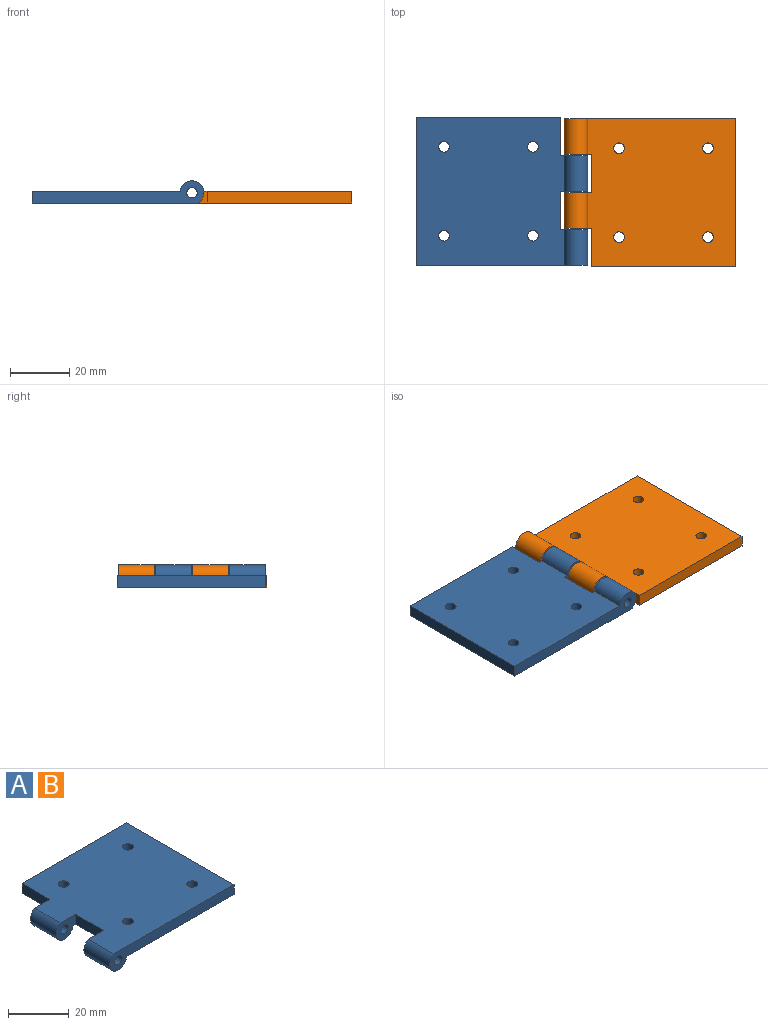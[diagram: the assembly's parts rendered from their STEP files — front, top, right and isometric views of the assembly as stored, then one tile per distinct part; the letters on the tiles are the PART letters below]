
ASSEMBLY  parts=2 mates=1
PART A: 18 faces, bbox 58x50x7.5 mm
  f0: plane 55.96x50mm, normal (0,0,1), area 2572.9mm2, adj f2,f3,f5,f6,f7,f8,f9,f10
  f1: plane 50x50mm, normal (0,0,-1), area 2429.7mm2, adj f2,f3,f5,f6,f7,f8,f9,f10
  f2: cylinder r=4mm len=12mm, axis (0,1,0), area 194.6mm2, adj f0,f1,f9,f13
  f3: cylinder r=4mm len=12mm, axis (0,1,0), area 194.6mm2, adj f0,f1,f7,f10
  f4: cylinder r=1.75mm len=12mm, axis (0,1,0), area 131.9mm2, adj f7,f10
  f5: plane 48.86x4mm, normal (0,1,0), area 195.5mm2, adj f0,f1,f6,f12
  f6: plane 50x4mm, normal (1,0,0), area 200mm2, adj f0,f1,f5,f7
  f7: plane 57.96x7.46mm, normal (0,-1,0), area 241.1mm2, adj f0,f1,f3,f4,f6
  f8: plane 13x4mm, normal (-1,0,0), area 52mm2, adj f0,f1,f9,f10
  f9: plane 9.1x7.46mm, normal (0,-1,0), area 45.6mm2, adj f0,f1,f2,f8,f11
  f10: plane 9.1x7.46mm, normal (0,1,0), area 45.6mm2, adj f0,f1,f3,f4,f8
  f11: cylinder r=1.75mm len=12mm, axis (0,1,0), area 131.9mm2, adj f9,f13
  f12: plane 13x4mm, normal (-1,0,0), area 52mm2, adj f0,f1,f5,f13
  f13: plane 9.1x7.46mm, normal (0,1,0), area 45.6mm2, adj f0,f1,f2,f11,f12
  f14: cylinder r=1.8mm len=4mm, axis (0,0,-1), area 45.2mm2, adj f0,f1
  f15: cylinder r=1.8mm len=4mm, axis (0,0,-1), area 45.2mm2, adj f0,f1
  f16: cylinder r=1.8mm len=4mm, axis (0,0,-1), area 45.2mm2, adj f0,f1
  f17: cylinder r=1.8mm len=4mm, axis (0,0,-1), area 45.2mm2, adj f0,f1
PART B: same geometry as A
PLACE A rot(axis=(0,-1,0),180deg) t=(-28.48,28.23,-16.57)mm
PLACE B rot(axis=(1,0,0),180deg) t=(-28.48,-22.27,-16.57)mm
MATE revolute A.f2 <-> B.f2  axis (0,1,0) through (-28.48,15.23,-16.57)mm
